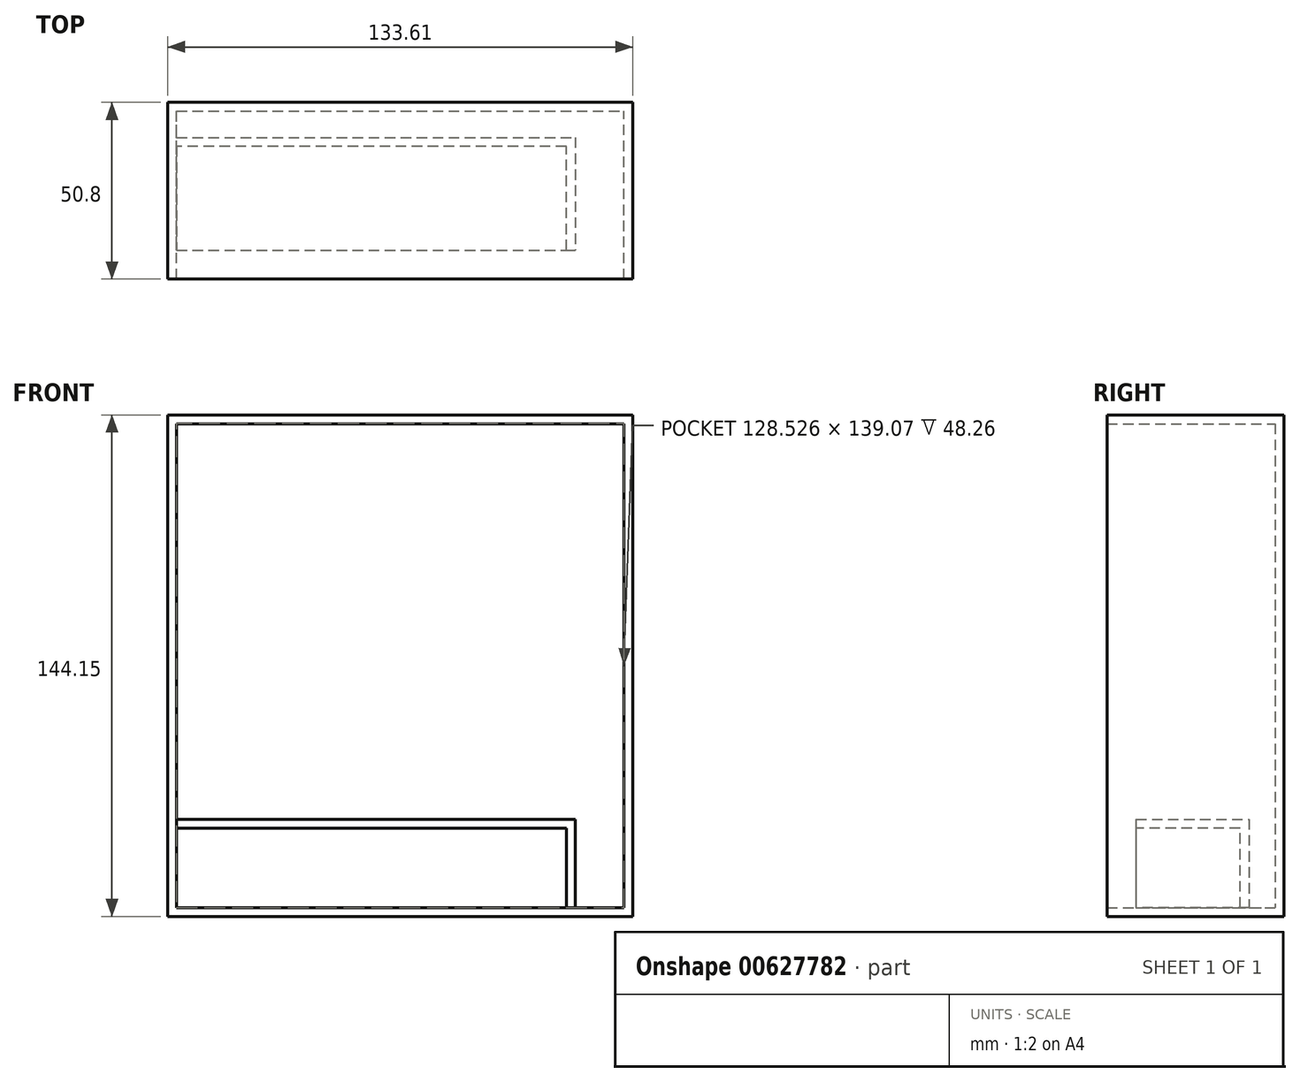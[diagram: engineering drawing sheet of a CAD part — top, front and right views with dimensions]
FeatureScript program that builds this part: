
annotation { "Feature Type Name" : "Feature", "Feature Type Description" : "" }
export const myFeature = defineFeature(function(context is Context, id is Id, definition is map)
    precondition{}
    {
        {
            var Q0;
            Q0=qCreatedBy(makeId("Front.planeOp"),FACE);
            var sketch = newSketch(context, id + "F0", { "sketchPlane" : qUnion([Q0])});
            skLineSegment(sketch, "E0.bottom", {"start": v(-71.16, 69.9) * mm, "end": v(62.45, 69.9) * mm});
            skLineSegment(sketch, "E0.top", {"start": v(-71.16, -74.26) * mm, "end": v(62.45, -74.26) * mm});
            skLineSegment(sketch, "E0.left", {"start": v(-71.16, 69.9) * mm, "end": v(-71.16, -74.26) * mm});
            skLineSegment(sketch, "E0.right", {"start": v(62.45, 69.9) * mm, "end": v(62.45, -74.26) * mm});
            skSolve(sketch);
        }
        {
            var Q0;
            Q0=makeQuery(id+"F0.imprint","IMPRINT",FACE,{"disambiguationData":[TD([[makeQuery(id+"F0.imprint","IMPRINT",EDGE,{"derivedFrom":sQuery(id+"F0.wireOp",EDGE,"E0.bottom")}),-1.0]])]});
            extrude(context, id + "F1", {"entities" : qUnion([Q0]), "depth" : 25.4 * mm, "offsetDistance" : 25.4 * mm, "hasSecondDirection" : true, "secondDirectionOppositeDirection" : true, "secondDirectionDepth" : 25.4 * mm});
        }
        {
            var Q0;
            Q0=makeQuery(id+"F1.opExtrude","CAP_FACE",FACE,{"disambiguationData":[OSD([sQuery(id+"F0.wireOp",EDGE,"E0.bottom"),sQuery(id+"F0.wireOp",EDGE,"E0.top"),sQuery(id+"F0.wireOp",EDGE,"E0.left"),sQuery(id+"F0.wireOp",EDGE,"E0.right")])],"isStart":false});
            shell(context, id + "F2", {"entities" : qUnion([Q0]), "thickness" : 2.54 * mm});
        }
        {
            var Q0;
            Q0=makeQuery(id+"F2.opShell","OFFSET_FACE",FACE,{"disambiguationData":[OSD([sQuery(id+"F0.wireOp",EDGE,"E0.top")])]});
            var sketch = newSketch(context, id + "F3", { "sketchPlane" : qUnion([Q0])});
            skLineSegment(sketch, "E1.bottom", {"start": v(-68.62, 15.34) * mm, "end": v(45.87, 15.34) * mm});
            skLineSegment(sketch, "E1.top", {"start": v(-68.62, -17.07) * mm, "end": v(45.87, -17.07) * mm});
            skLineSegment(sketch, "E1.left", {"start": v(-68.62, 15.34) * mm, "end": v(-68.62, -17.07) * mm});
            skLineSegment(sketch, "E1.right", {"start": v(45.87, 15.34) * mm, "end": v(45.87, -17.07) * mm});
            skSolve(sketch);
        }
        {
            var Q0;
            Q0=makeQuery(id+"F3.imprint","IMPRINT",FACE,{"disambiguationData":[TD([[makeQuery(id+"F3.imprint","IMPRINT",EDGE,{"derivedFrom":sQuery(id+"F3.wireOp",EDGE,"E1.bottom")}),-1.0]])]});
            extrude(context, id + "F4", {"entities" : qUnion([Q0]), "operationType" : NewBodyOperationType.ADD, "depth" : 25.4 * mm, "offsetDistance" : 25.4 * mm});
        }
        {
            var Q0;
            Q0=makeQuery(id+"F4.opExtrude","SWEPT_FACE",FACE,{"disambiguationData":[OSD([sQuery(id+"F3.wireOp",EDGE,"E1.top")])]});
            shell(context, id + "F5", {"entities" : qUnion([Q0]), "thickness" : 2.54 * mm});
        }
    });
